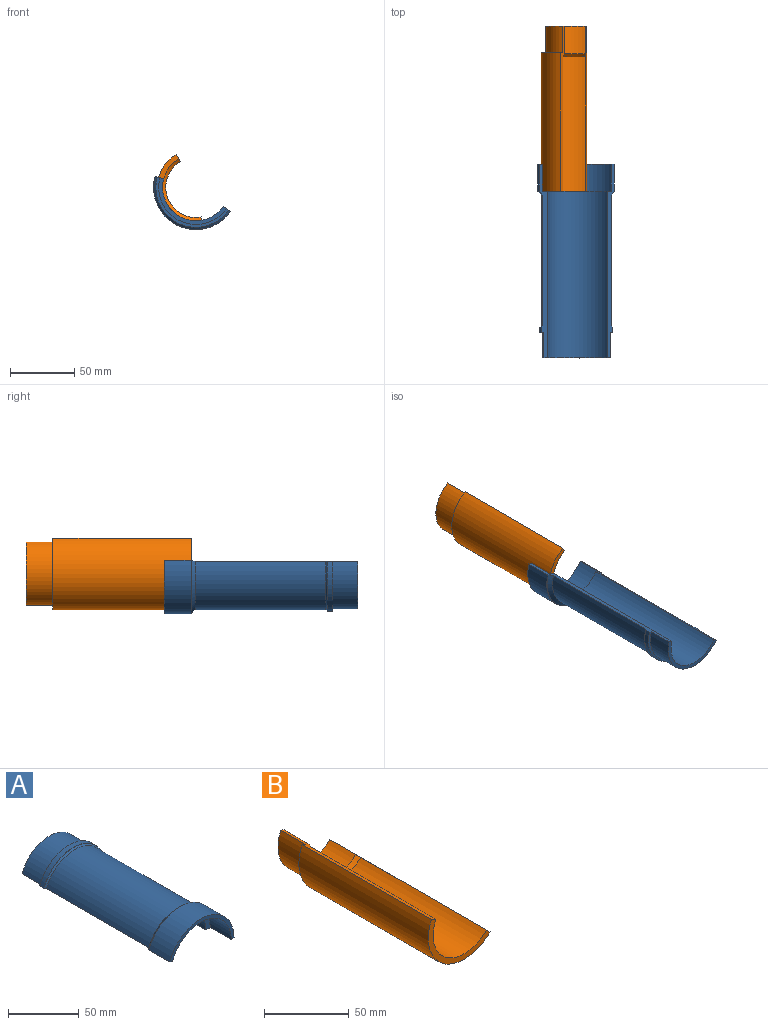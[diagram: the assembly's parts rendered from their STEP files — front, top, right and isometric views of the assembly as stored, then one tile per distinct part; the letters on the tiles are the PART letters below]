
ASSEMBLY  parts=2 mates=1
PART A: 16 faces, bbox 64x151.2x33 mm
  f0: cylinder r=26mm len=130.2mm, axis (0,1,0), area 9453.3mm2, adj f2,f13,f14,f15
  f1: cylinder r=29.8mm len=102mm, axis (0,1,0), area 8488.2mm2, adj f5,f11,f14,f15
  f2: plane 56.25x29mm, normal (0,1,0), area 230.4mm2, adj f0,f6,f14,f15
  f3: cylinder r=31.2mm len=60.52mm, axis (0,1,0), area 365.9mm2, adj f4,f7,f14,f15
  f4: plane 60.52x31.2mm, normal (0,-1,0), area 17.4mm2, adj f3,f5,f14,f15
  f5: cone r=31mm half-angle=45deg, axis (0,1,0), area 144.1mm2, adj f1,f4,f14,f15
  f6: cylinder r=29mm len=56.25mm, axis (0,1,0), area 1603.5mm2, adj f2,f7,f14,f15
  f7: plane 60.52x31.2mm, normal (0,1,0), area 184.9mm2, adj f3,f6,f14,f15
  f8: plane 64.01x33mm, normal (0,-1,0), area 247.1mm2, adj f9,f12,f14,f15
  f9: cylinder r=33mm len=64.01mm, axis (0,-1,0), area 1935.2mm2, adj f8,f10,f14,f15
  f10: plane 64.01x33mm, normal (0,1,0), area 18.4mm2, adj f9,f11,f14,f15
  f11: cone r=32.8mm half-angle=45deg, axis (0,-1,0), area 370.8mm2, adj f1,f10,f14,f15
  f12: cylinder r=30.2mm len=58.58mm, axis (0,-1,0), area 1771mm2, adj f8,f13,f14,f15
  f13: plane 58.58x30.2mm, normal (0,-1,0), area 329.6mm2, adj f0,f12,f14,f15
  f14: plane 151.2x6.58mm, normal (-0.34,0,-0.94), area 548.8mm2, adj f0,f1,f2,f3,f4,f5,f6,f7
  f15: plane 151.2x7mm, normal (0,0,-1), area 548.8mm2, adj f0,f1,f2,f3,f4,f5,f6,f7
PART B: 10 faces, bbox 51.5x129x42.4 mm
  f0: cylinder r=23.5mm len=40.31mm, axis (0,-1,0), area 1410.9mm2, adj f5,f6,f8,f9
  f1: cylinder r=26mm len=105mm, axis (0,1,0), area 7623.6mm2, adj f2,f6,f8,f9
  f2: plane 51.46x42.36mm, normal (0,-1,0), area 312.8mm2, adj f1,f7,f8,f9
  f3: plane 51.46x42.36mm, normal (0,1,0), area 276.1mm2, adj f4,f7,f8,f9
  f4: cylinder r=26.5mm len=45.45mm, axis (0,-1,0), area 1554mm2, adj f3,f5,f8,f9
  f5: plane 45.45x37.42mm, normal (0,1,0), area 209.4mm2, adj f0,f4,f8,f9
  f6: cone r=23mm half-angle=45deg, axis (0,-1,0), area 244.4mm2, adj f0,f1,f8,f9
  f7: cylinder r=30mm len=108mm, axis (0,1,0), area 9047.8mm2, adj f2,f3,f8,f9
  f8: plane 129x4.65mm, normal (0.7,0,0.72), area 499.4mm2, adj f0,f1,f2,f3,f4,f5,f6,f7
  f9: plane 129x5.92mm, normal (0.41,0,0.91), area 499.4mm2, adj f0,f1,f2,f3,f4,f5,f6,f7
PLACE A rot(axis=(-0.95,0,0.3),180deg) t=(-10.47,-269.04,-6.53)mm
PLACE B rot(axis=(0,1,0),35deg) t=(-10.47,-30.84,-6.53)mm
MATE fastened B.f7 <-> A.f12  axis (0,-1,0) through (-10.47,-138.84,-6.53)mm
